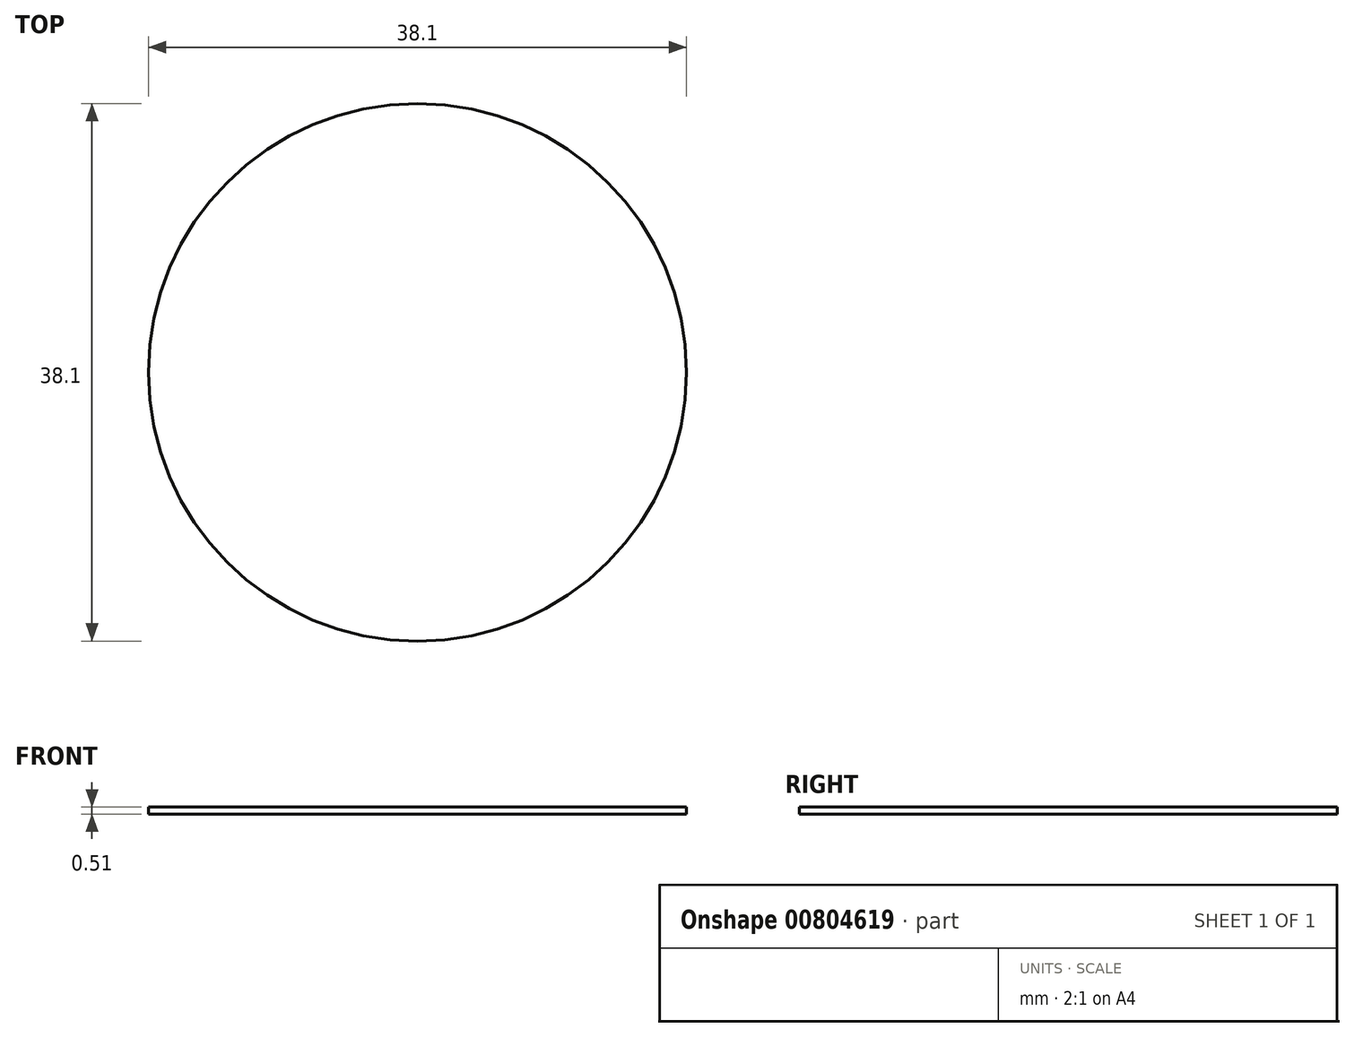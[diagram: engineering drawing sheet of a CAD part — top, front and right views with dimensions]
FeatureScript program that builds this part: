
annotation { "Feature Type Name" : "Feature", "Feature Type Description" : "" }
export const myFeature = defineFeature(function(context is Context, id is Id, definition is map)
    precondition{}
    {
        {
            var Q0;
            Q0=qCreatedBy(makeId("Top.planeOp"),FACE);
            cPlane(context, id + "F0", {"entities" : qUnion([Q0]), "cplaneType" : CPlaneType.OFFSET, "offset" : 76.2 * mm, "width" : 152.4 * mm, "height" : 152.4 * mm});
        }
        {
            var Q0;
            Q0=qCreatedBy(makeId("Top.planeOp"),FACE);
            var sketch = newSketch(context, id + "F1", { "sketchPlane" : qUnion([Q0])});
            skCircle(sketch, "E0", {"center": v(0, 0) * mm, "radius": 19.05 * mm});
            skSolve(sketch);
        }
        {
            var Q0;
            Q0=qCreatedBy(id+"F0.planeOp",FACE);
            var sketch = newSketch(context, id + "F2", { "sketchPlane" : qUnion([Q0])});
            skCircle(sketch, "E1", {"center": v(0, 0) * mm, "radius": 31.75 * mm});
            skSolve(sketch);
        }
        {
            var Q0;
            Q0=qSketchRegion(id+"F1",true);
            extrude(context, id + "F3", {"entities" : qUnion([Q0]), "depth" : 0.5 * mm, "offsetDistance" : 25.4 * mm});
        }
        {
            var Q0;
            Q0=makeQuery(id+"F2.imprint","IMPRINT",FACE,{"disambiguationData":[TD([[makeQuery(id+"F2.imprint","IMPRINT",EDGE,{"derivedFrom":sQuery(id+"F2.wireOp",EDGE,"E1")}),1.0]])]});
            var Q1;
            Q1=makeQuery(id+"F1.imprint","IMPRINT",FACE,{"disambiguationData":[TD([[makeQuery(id+"F1.imprint","IMPRINT",EDGE,{"derivedFrom":sQuery(id+"F1.wireOp",EDGE,"E0")}),1.0]])]});
            var Q2;
            Q2=sQuery(id+"F2.wireOp",EDGE,"E1");
            var Q3;
            Q3=makeQuery(id+"F3.opExtrude","CAP_EDGE",EDGE,{"disambiguationData":[OSD([sQuery(id+"F1.wireOp",EDGE,"E0")])],"isStart":false});
            loft(context, id + "F4", {"bodyType" : ToolBodyType.SURFACE, "sheetProfilesArray" : [{ "sheetProfileEntities" : qUnion([Q0]) }, { "sheetProfileEntities" : qUnion([Q1]) }], "wireProfilesArray" : [{ "wireProfileEntities" : qUnion([Q2]) }, { "wireProfileEntities" : qUnion([Q3]) }]});
        }
    });
